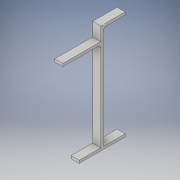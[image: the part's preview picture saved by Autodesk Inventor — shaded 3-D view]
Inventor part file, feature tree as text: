
AUTODESK INVENTOR PART (.ipt)
format: ipt  version: 2017 (Build 210142000, 142)  size: 141,312 bytes
history: native  units: in
note: dims shown in document units (in); Inventor stores cm internally (conversion verified against a paired STEP export)
features: sketch x6, extrude x5, fillet x1
ambient origin geometry x8: Origin, YZ Plane, XZ Plane, XY Plane, X Axis, Y Axis, Z Axis, Center Point
bodies: Solid1 (feature_tree)
feature tree (12):
  extrude  "Extrusion1"  Depth=10.0in
  sketch  "Sketch4"  dims[d2=0.25in d3=0.0in d4=1.25in]
  extrude  "Extrusion2"  Depth=1.25in
  extrude  "Extrusion3"  Depth=3.5in TaperAngle=0.0deg
  fillet  "Fillet2"  Radius=0.25in
  extrude  "Extrusion4"  Depth=0.25in
  extrude  "Extrusion5"  Depth=0.25in
  sketch  "Sketch3"  dims[d0=0.75in d1=10.0in]
  sketch  "Sketch5"  dims[d5=0.25in d6=3.5in d7=0.0in d8=0.25in]
  sketch  "Sketch6"  dims[d9=2.0in d10=0.0in d12=0.25in]
  sketch  "Sketch7"  dims[d13=0.75in d14=0.25in]
  sketch  "Sketch8"  dims[d15=2.0in d16=0.0in d17=0.25in d18=2.0in d19=0.0in]
